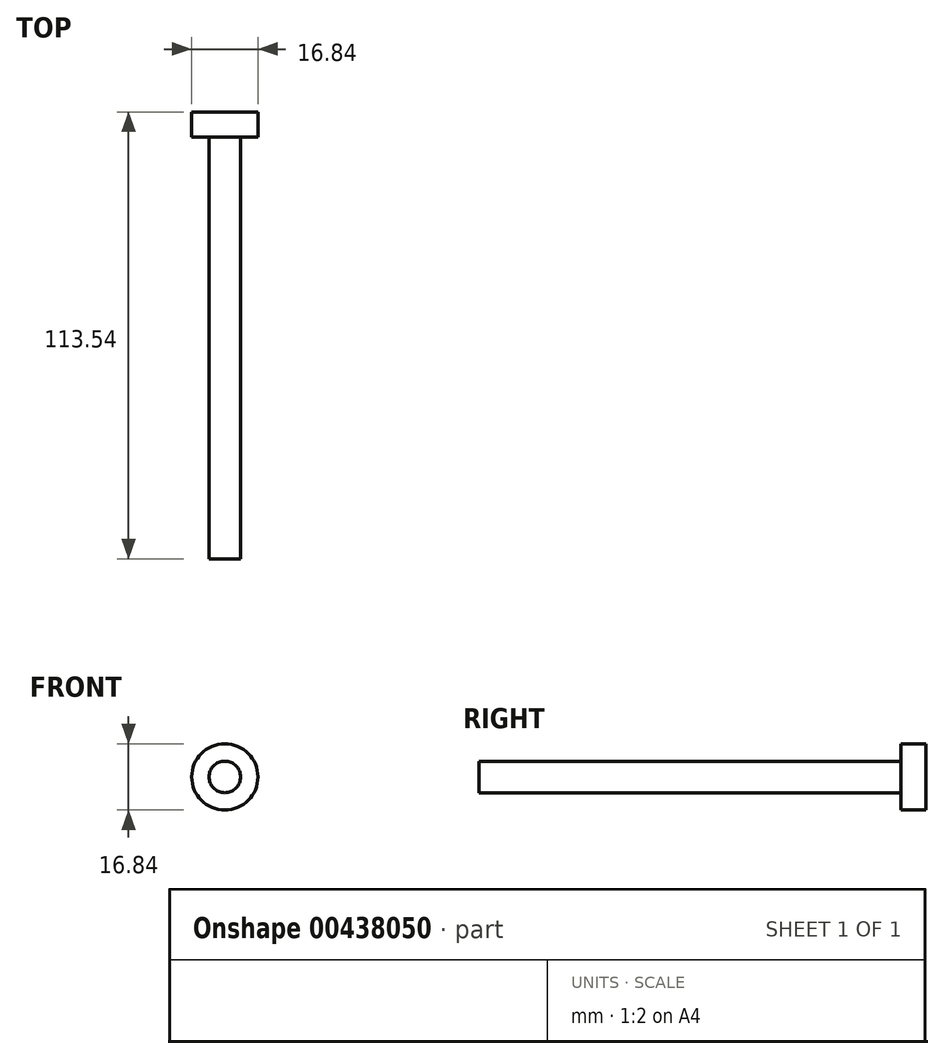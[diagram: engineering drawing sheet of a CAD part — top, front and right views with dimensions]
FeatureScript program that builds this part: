
annotation { "Feature Type Name" : "Feature", "Feature Type Description" : "" }
export const myFeature = defineFeature(function(context is Context, id is Id, definition is map)
    precondition{}
    {
        {
            var Q0;
            Q0=qCreatedBy(makeId("Front.planeOp"),FACE);
            var sketch = newSketch(context, id + "F0", { "sketchPlane" : qUnion([Q0])});
            skCircle(sketch, "E0", {"center": v(0, 0) * mm, "radius": 4 * mm});
            skSolve(sketch);
        }
        {
            var Q0;
            Q0=makeQuery(id+"F0.imprint","IMPRINT",FACE,{"disambiguationData":[TD([[makeQuery(id+"F0.imprint","IMPRINT",EDGE,{"derivedFrom":sQuery(id+"F0.wireOp",EDGE,"E0")}),1.0]])]});
            var Q1;
            Q1=sQuery(id+"F0.wireOp",EDGE,"E0");
            extrude(context, id + "F1", {"entities" : qUnion([Q0]), "surfaceEntities" : qUnion([Q1]), "depth" : 107.19 * mm});
        }
        {
            var Q0;
            Q0=qCreatedBy(makeId("Front.planeOp"),FACE);
            var sketch = newSketch(context, id + "F2", { "sketchPlane" : qUnion([Q0])});
            skCircle(sketch, "E1", {"center": v(0, 0) * mm, "radius": 8.42 * mm});
            skSolve(sketch);
        }
        {
            var Q0;
            Q0=makeQuery(id+"F2.imprint","IMPRINT",FACE,{"disambiguationData":[TD([[makeQuery(id+"F2.imprint","IMPRINT",EDGE,{"derivedFrom":sQuery(id+"F2.wireOp",EDGE,"E1")}),1.0]])]});
            var Q1;
            Q1=sQuery(id+"F2.wireOp",EDGE,"E1");
            extrude(context, id + "F3", {"entities" : qUnion([Q0]), "operationType" : NewBodyOperationType.ADD, "surfaceEntities" : qUnion([Q1]), "depth" : -6.35 * mm});
        }
    });
